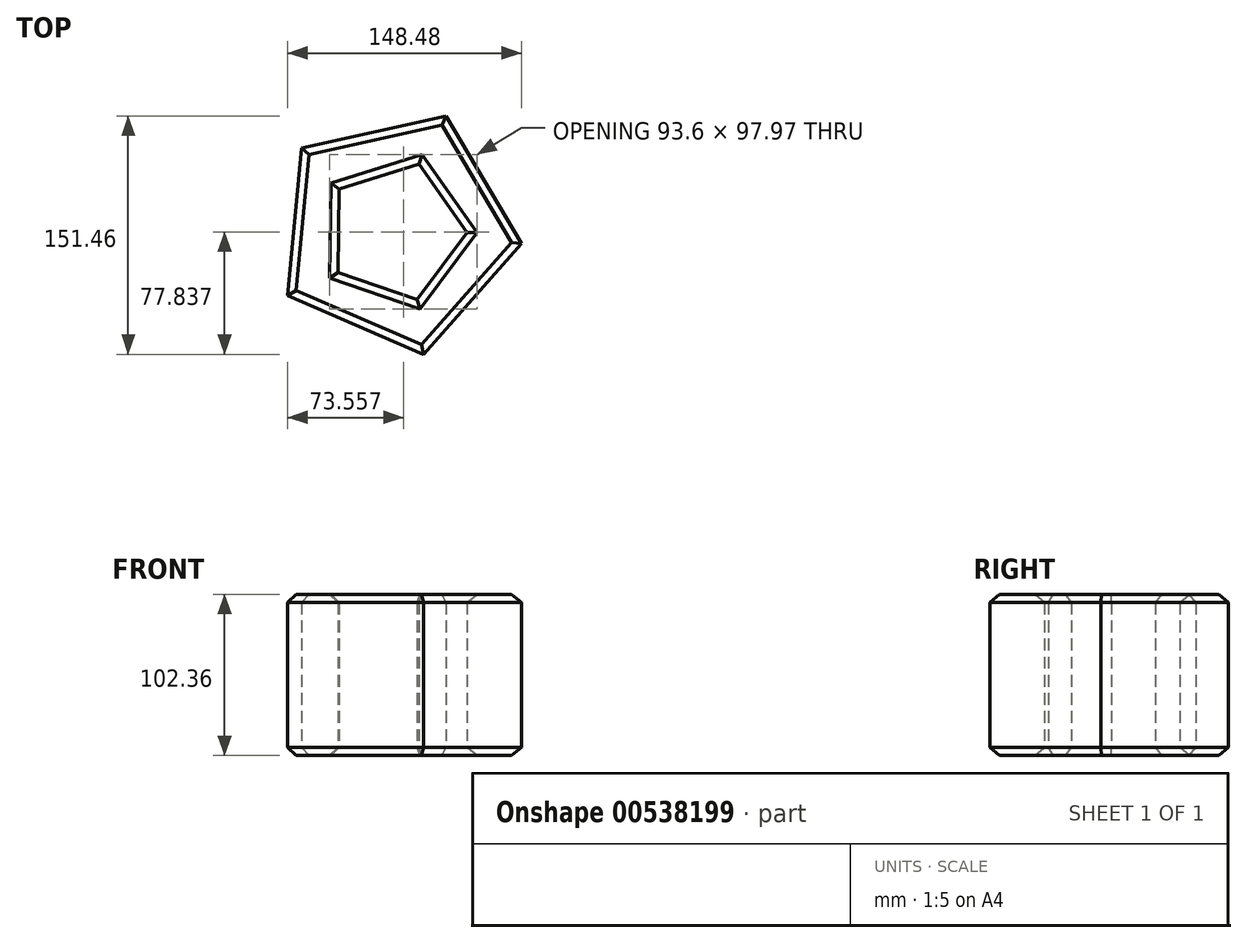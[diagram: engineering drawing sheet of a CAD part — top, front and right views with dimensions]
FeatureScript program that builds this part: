
annotation { "Feature Type Name" : "Feature", "Feature Type Description" : "" }
export const myFeature = defineFeature(function(context is Context, id is Id, definition is map)
    precondition{}
    {
        {
            var Q0;
            Q0=qCreatedBy(makeId("Top.planeOp"),FACE);
            var sketch = newSketch(context, id + "F0", { "sketchPlane" : qUnion([Q0])});
            skCircle(sketch, "E0.cCircle", {"center": v(0, 0) * mm, "radius": 64.71 * mm, "construction": true});
            skLineSegment(sketch, "E0.0", {"start": v(79.63, -7.54) * mm, "end": v(17.44, -78.06) * mm});
            skLineSegment(sketch, "E0.1", {"start": v(17.44, -78.06) * mm, "end": v(-68.85, -40.7) * mm});
            skLineSegment(sketch, "E0.2", {"start": v(-68.85, -40.7) * mm, "end": v(-60, 52.9) * mm});
            skLineSegment(sketch, "E0.3", {"start": v(-60, 52.9) * mm, "end": v(31.78, 73.4) * mm});
            skLineSegment(sketch, "E0.4", {"start": v(31.78, 73.4) * mm, "end": v(79.63, -7.54) * mm});
            skPoint(sketch, "E0.0.midPoint", {"position": v(48.54, -42.8) * mm});
            skCircle(sketch, "E1.cCircle", {"center": v(0, 0) * mm, "radius": 36.6 * mm, "construction": true});
            skLineSegment(sketch, "E1.0", {"start": v(45.23, -0.63) * mm, "end": v(13.37, -43.2) * mm});
            skLineSegment(sketch, "E1.1", {"start": v(13.37, -43.2) * mm, "end": v(-36.96, -26.07) * mm});
            skLineSegment(sketch, "E1.2", {"start": v(-36.96, -26.07) * mm, "end": v(-36.22, 27.1) * mm});
            skLineSegment(sketch, "E1.3", {"start": v(-36.22, 27.1) * mm, "end": v(14.58, 42.82) * mm});
            skLineSegment(sketch, "E1.4", {"start": v(14.58, 42.82) * mm, "end": v(45.23, -0.63) * mm});
            skPoint(sketch, "E1.0.midPoint", {"position": v(29.3, -21.92) * mm});
            skSolve(sketch);
        }
        {
            var Q0;
            Q0=makeQuery(id+"F0.imprint","IMPRINT",FACE,{"disambiguationData":[TD([[makeQuery(id+"F0.imprint","IMPRINT",EDGE,{"derivedFrom":sQuery(id+"F0.wireOp",EDGE,"E0.0")}),-1.0]])]});
            extrude(context, id + "F1", {"entities" : qUnion([Q0]), "depth" : 102.36 * mm, "offsetDistance" : 25.4 * mm});
        }
        {
            var Q0;
            Q0=makeQuery(id+"F1.opExtrude","CAP_FACE",FACE,{"disambiguationData":[OSD([sQuery(id+"F0.wireOp",EDGE,"E0.0"),sQuery(id+"F0.wireOp",EDGE,"E0.1"),sQuery(id+"F0.wireOp",EDGE,"E0.2"),sQuery(id+"F0.wireOp",EDGE,"E0.3"),sQuery(id+"F0.wireOp",EDGE,"E0.4"),sQuery(id+"F0.wireOp",EDGE,"E1.0"),sQuery(id+"F0.wireOp",EDGE,"E1.1"),sQuery(id+"F0.wireOp",EDGE,"E1.2"),sQuery(id+"F0.wireOp",EDGE,"E1.3"),sQuery(id+"F0.wireOp",EDGE,"E1.4")])],"isStart":true});
            var Q1;
            Q1=makeQuery(id+"F1.opExtrude","CAP_FACE",FACE,{"disambiguationData":[OSD([sQuery(id+"F0.wireOp",EDGE,"E0.0"),sQuery(id+"F0.wireOp",EDGE,"E0.1"),sQuery(id+"F0.wireOp",EDGE,"E0.2"),sQuery(id+"F0.wireOp",EDGE,"E0.3"),sQuery(id+"F0.wireOp",EDGE,"E0.4"),sQuery(id+"F0.wireOp",EDGE,"E1.0"),sQuery(id+"F0.wireOp",EDGE,"E1.1"),sQuery(id+"F0.wireOp",EDGE,"E1.2"),sQuery(id+"F0.wireOp",EDGE,"E1.3"),sQuery(id+"F0.wireOp",EDGE,"E1.4")])],"isStart":false});
            chamfer(context, id + "F2", {"entities" : qUnion([Q0, Q1]), "width" : 5.08 * mm, "tangentPropagation" : true});
        }
    });
